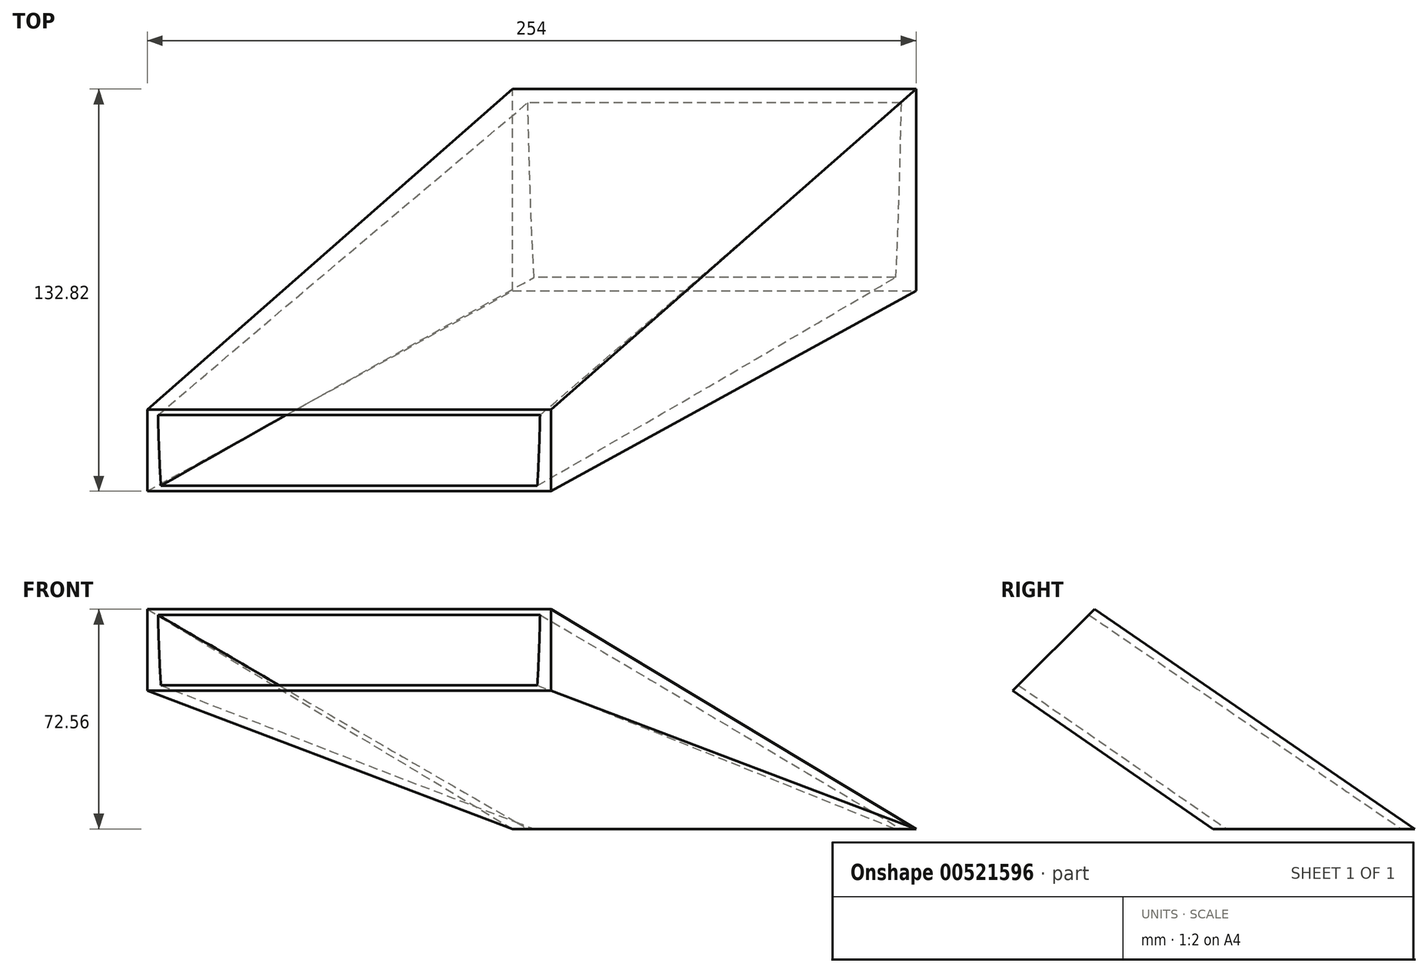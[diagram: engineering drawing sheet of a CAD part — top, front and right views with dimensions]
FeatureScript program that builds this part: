
annotation { "Feature Type Name" : "Feature", "Feature Type Description" : "" }
export const myFeature = defineFeature(function(context is Context, id is Id, definition is map)
    precondition{}
    {
        {
            var Q0;
            Q0=qCreatedBy(makeId("Top.planeOp"),FACE);
            var sketch = newSketch(context, id + "F0", { "sketchPlane" : qUnion([Q0])});
            skLineSegment(sketch, "E0.bottom", {"start": v(0, 0) * mm, "end": v(120.65, 0) * mm, "construction": true});
            skLineSegment(sketch, "E0.top", {"start": v(0, 53.98) * mm, "end": v(120.65, 53.98) * mm, "construction": true});
            skLineSegment(sketch, "E0.left", {"start": v(0, 0) * mm, "end": v(0, 53.98) * mm, "construction": true});
            skLineSegment(sketch, "E0.right", {"start": v(120.65, 0) * mm, "end": v(120.65, 53.98) * mm, "construction": true});
            skLineSegment(sketch, "E1.0", {"start": v(-6.35, -6.35) * mm, "end": v(127, -6.35) * mm});
            skLineSegment(sketch, "E1.1", {"start": v(-6.35, -6.35) * mm, "end": v(-6.35, 60.33) * mm});
            skLineSegment(sketch, "E1.2", {"start": v(-6.35, 60.33) * mm, "end": v(127, 60.33) * mm});
            skLineSegment(sketch, "E1.3", {"start": v(127, -6.35) * mm, "end": v(127, 60.33) * mm});
            skSolve(sketch);
        }
        {
            var Q0;
            Q0=qCreatedBy(makeId("Top.planeOp"),FACE);
            cPlane(context, id + "F1", {"entities" : qUnion([Q0]), "cplaneType" : CPlaneType.OFFSET, "offset" : 55.88 * mm, "width" : 152.4 * mm, "height" : 152.4 * mm});
        }
        {
            var Q0;
            Q0=qCreatedBy(id+"F1.planeOp",FACE);
            var sketch = newSketch(context, id + "F2", { "sketchPlane" : qUnion([Q0])});
            skLineSegment(sketch, "E2.0", {"start": v(-6.35, -6.35) * mm, "end": v(127, -6.35) * mm, "construction": true});
            skLineSegment(sketch, "E3.0", {"start": v(-6.35, -62.23) * mm, "end": v(127, -62.23) * mm});
            skSolve(sketch);
        }
        {
            var Q0;
            Q0=qCreatedBy(id+"F1.planeOp",FACE);
            var Q1;
            Q1=sQuery(id+"F2.wireOp",EDGE,"E3.0");
            cPlane(context, id + "F3", {"entities" : qUnion([Q0, Q1]), "cplaneType" : CPlaneType.LINE_ANGLE, "offset" : 25.4 * mm, "angle" : 45 * degree, "width" : 152.4 * mm, "height" : 152.4 * mm});
        }
        {
            var Q0;
            Q0=qCreatedBy(id+"F3.planeOp",FACE);
            var sketch = newSketch(context, id + "F4", { "sketchPlane" : qUnion([Q0])});
            skLineSegment(sketch, "E4.0", {"start": v(-6.35, 4.5) * mm, "end": v(127, 4.5) * mm, "construction": true});
            skLineSegment(sketch, "E5.bottom", {"start": v(-6.35, -19) * mm, "end": v(127, -19) * mm});
            skLineSegment(sketch, "E5.top", {"start": v(-6.35, 19.1) * mm, "end": v(127, 19.1) * mm});
            skLineSegment(sketch, "E5.left", {"start": v(-6.35, -19) * mm, "end": v(-6.35, 19.1) * mm});
            skLineSegment(sketch, "E5.right", {"start": v(127, -19) * mm, "end": v(127, 19.1) * mm});
            skLineSegment(sketch, "E6.0", {"start": v(-1.27, -13.92) * mm, "end": v(-1.27, 14.02) * mm, "construction": true});
            skLineSegment(sketch, "E6.1", {"start": v(-1.27, -13.92) * mm, "end": v(121.92, -13.92) * mm, "construction": true});
            skLineSegment(sketch, "E6.2", {"start": v(121.92, -13.92) * mm, "end": v(121.92, 14.02) * mm, "construction": true});
            skLineSegment(sketch, "E6.3", {"start": v(-1.27, 14.02) * mm, "end": v(121.92, 14.02) * mm, "construction": true});
            skSolve(sketch);
        }
        {
            var Q0;
            Q0=makeQuery(id+"F4.imprint","IMPRINT",FACE,{"disambiguationData":[TD([[makeQuery(id+"F4.imprint","IMPRINT",EDGE,{"derivedFrom":sQuery(id+"F4.wireOp",EDGE,"E5.bottom")}),1.0]])]});
            var Q1;
            Q1=makeQuery(id+"F0.imprint","IMPRINT",FACE,{"disambiguationData":[TD([[makeQuery(id+"F0.imprint","IMPRINT",EDGE,{"derivedFrom":sQuery(id+"F0.wireOp",EDGE,"E1.0")}),1.0]])]});
            loft(context, id + "F5", {"sheetProfilesArray" : [{ "sheetProfileEntities" : qUnion([Q0]) }, { "sheetProfileEntities" : qUnion([Q1]) }]});
        }
        {
            var Q0;
            Q0=makeQuery(id+"F5.opLoft","CAP_FACE",FACE,{"disambiguationData":[OSD([makeQuery(id+"F0.imprint","IMPRINT",FACE,{"disambiguationData":[TD([[makeQuery(id+"F0.imprint","IMPRINT",EDGE,{"derivedFrom":sQuery(id+"F0.wireOp",EDGE,"E1.0")}),1.0]])]})])],"isStart":true});
            var Q1;
            Q1=makeQuery(id+"F5.opLoft","CAP_FACE",FACE,{"disambiguationData":[OSD([makeQuery(id+"F4.imprint","IMPRINT",FACE,{"disambiguationData":[TD([[makeQuery(id+"F4.imprint","IMPRINT",EDGE,{"derivedFrom":sQuery(id+"F4.wireOp",EDGE,"E5.bottom")}),1.0]])]})])],"isStart":true});
            shell(context, id + "F6", {"entities" : qUnion([Q0, Q1]), "thickness" : 2.54 * mm});
        }
    });
